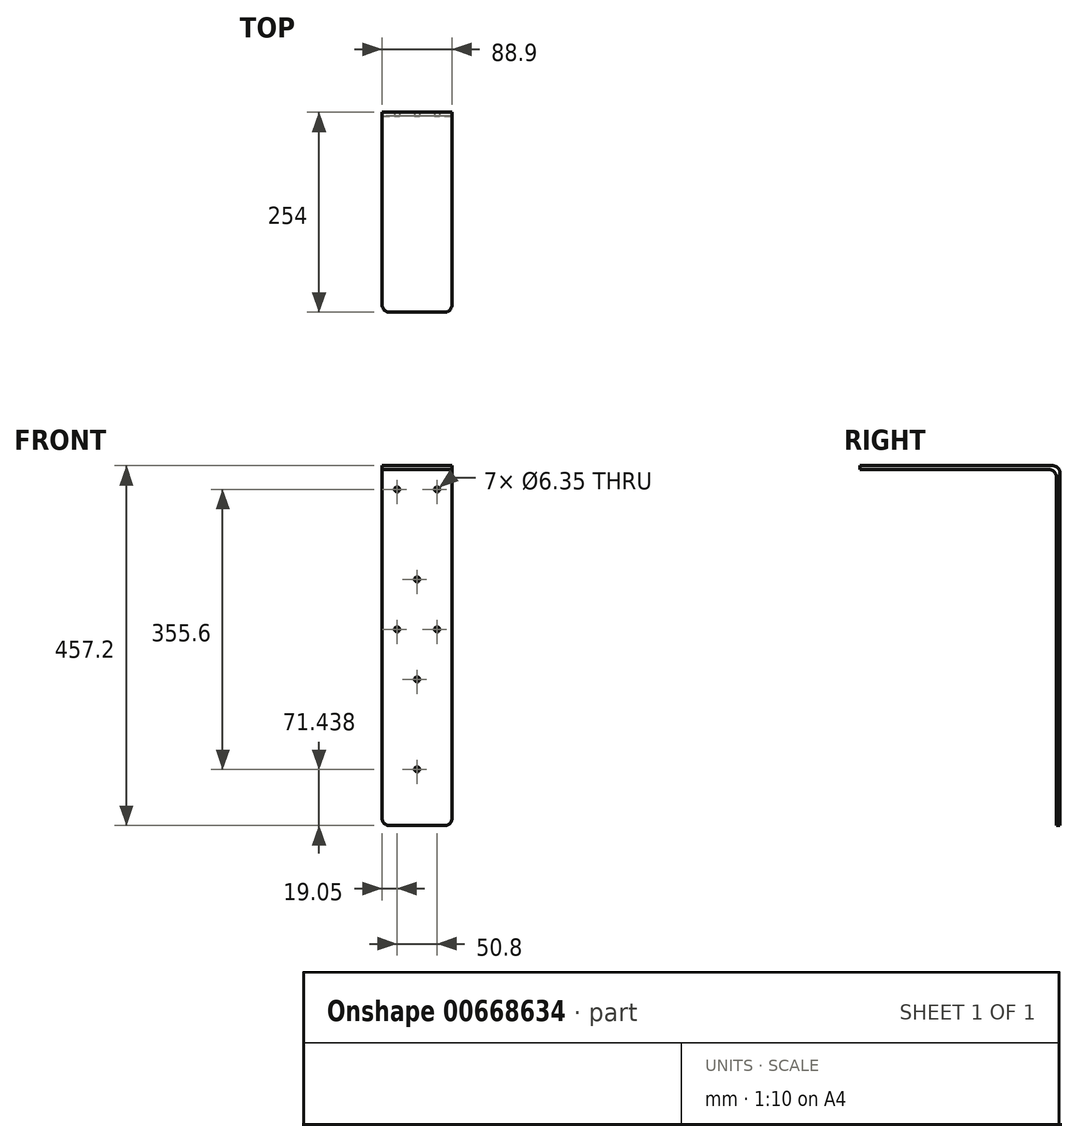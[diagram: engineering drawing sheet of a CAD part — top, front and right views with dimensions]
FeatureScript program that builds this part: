
annotation { "Feature Type Name" : "Feature", "Feature Type Description" : "" }
export const myFeature = defineFeature(function(context is Context, id is Id, definition is map)
    precondition{}
    {
        {
            var Q0;
            Q0=qCreatedBy(makeId("Right.planeOp"),FACE);
            var sketch = newSketch(context, id + "F0", { "sketchPlane" : qUnion([Q0]), "disableImprinting" : false});
            skLineSegment(sketch, "E0", {"start": v(-127, 0) * mm, "end": v(127, 0) * mm});
            skLineSegment(sketch, "E1", {"start": v(127, 0) * mm, "end": v(127, -457.2) * mm});
            skLineSegment(sketch, "E2", {"start": v(127, -457.2) * mm, "end": v(122.24, -457.2) * mm});
            skLineSegment(sketch, "E3", {"start": v(122.24, -457.2) * mm, "end": v(122.24, -4.76) * mm});
            skLineSegment(sketch, "E4", {"start": v(122.24, -4.76) * mm, "end": v(-127, -4.76) * mm});
            skLineSegment(sketch, "E5", {"start": v(-127, -4.76) * mm, "end": v(-127, 0) * mm});
            skSolve(sketch);
        }
        {
            var Q0;
            Q0 = qSketchRegion(id + "F0", true);
            extrude(context, id + "F1", {"entities" : qUnion([Q0]), "depth" : 88.9 * mm, "offsetDistance" : 25.4 * mm, "symmetric" : true});
        }
        {
            var Q0;
            Q0=makeQuery(id+"F1.opExtrude","SWEPT_EDGE",EDGE,{"disambiguationData":[OSD([sQuery(id+"F0.wireOp",EDGE,"E0"),sQuery(id+"F0.wireOp",EDGE,"E1")])]});
            var Q1;
            Q1=makeQuery(id+"F1.opExtrude","SWEPT_EDGE",EDGE,{"disambiguationData":[OSD([sQuery(id+"F0.wireOp",EDGE,"E3"),sQuery(id+"F0.wireOp",EDGE,"E4")])]});
            var Q2;
            Q2=makeQuery(id+"F1.opExtrude","CAP_EDGE",EDGE,{"disambiguationData":[OSD([sQuery(id+"F0.wireOp",EDGE,"E5")])],"isStart":false});
            var Q3;
            Q3=makeQuery(id+"F1.opExtrude","CAP_EDGE",EDGE,{"disambiguationData":[OSD([sQuery(id+"F0.wireOp",EDGE,"E5")])],"isStart":true});
            var Q4;
            Q4=makeQuery(id+"F1.opExtrude","CAP_EDGE",EDGE,{"disambiguationData":[OSD([sQuery(id+"F0.wireOp",EDGE,"E2")])],"isStart":true});
            var Q5;
            Q5=makeQuery(id+"F1.opExtrude","CAP_EDGE",EDGE,{"disambiguationData":[OSD([sQuery(id+"F0.wireOp",EDGE,"E2")])],"isStart":false});
            fillet(context, id + "F2", {"entities" : qUnion([Q0, Q1, Q2, Q3, Q4, Q5]), "radius" : 9.52 * mm, "tangentPropagation" : true, "allowEdgeOverflow" : false});
        }
        {
            var Q0;
            Q0=makeQuery(id+"F1.opExtrude","SWEPT_FACE",FACE,{"disambiguationData":[OSD([sQuery(id+"F0.wireOp",EDGE,"E3")])]});
            var sketch = newSketch(context, id + "F3", { "sketchPlane" : qUnion([Q0]), "disableImprinting" : false});
            skCircle(sketch, "E6", {"center": v(-25.4, -30.16) * mm, "radius": 3.18 * mm});
            skCircle(sketch, "E7", {"center": v(25.4, -30.16) * mm, "radius": 3.18 * mm});
            skCircle(sketch, "E8", {"center": v(-25.4, -207.96) * mm, "radius": 3.18 * mm});
            skCircle(sketch, "E9", {"center": v(25.4, -207.96) * mm, "radius": 3.18 * mm});
            skCircle(sketch, "E10", {"center": v(0, -144.46) * mm, "radius": 3.18 * mm});
            skCircle(sketch, "E11", {"center": v(0, -385.76) * mm, "radius": 3.18 * mm});
            skCircle(sketch, "E12", {"center": v(0, -271.46) * mm, "radius": 3.18 * mm});
            skSolve(sketch);
        }
        {
            var Q0;
            Q0 = qSketchRegion(id + "F3", true);
            extrude(context, id + "F4", {"entities" : qUnion([Q0]), "operationType" : NewBodyOperationType.REMOVE, "endBound" : BoundingType.THROUGH_ALL, "oppositeDirection" : true, "depth" : 25.4 * mm, "offsetDistance" : 25.4 * mm});
        }
    });
